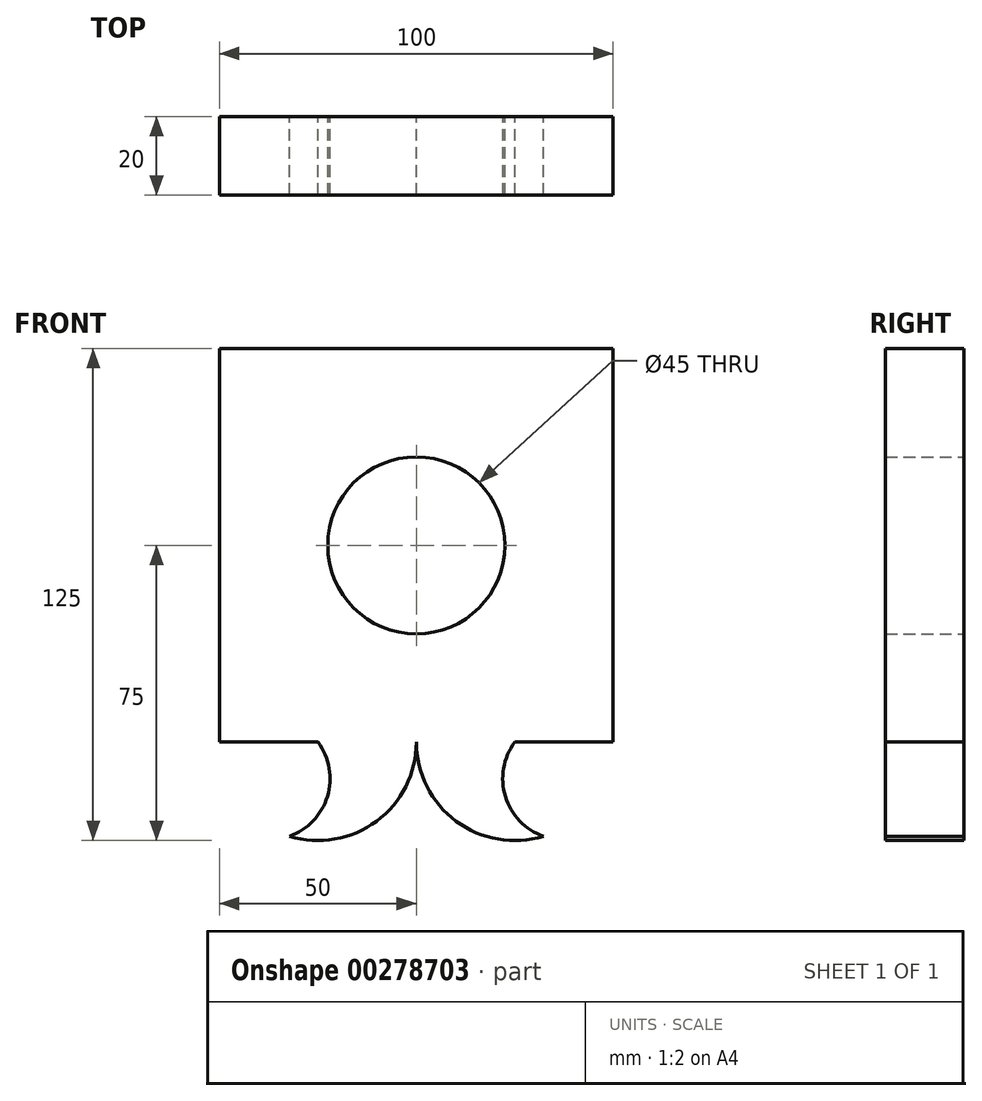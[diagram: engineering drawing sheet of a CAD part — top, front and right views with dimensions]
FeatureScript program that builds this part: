
annotation { "Feature Type Name" : "Feature", "Feature Type Description" : "" }
export const myFeature = defineFeature(function(context is Context, id is Id, definition is map)
    precondition{}
    {
        {
            var Q0;
            Q0=qCreatedBy(makeId("Front.planeOp"),FACE);
            var sketch = newSketch(context, id + "F0", { "sketchPlane" : qUnion([Q0])});
            skLineSegment(sketch, "E0.bottom", {"start": v(-40, 50) * mm, "end": v(40, 50) * mm});
            skLineSegment(sketch, "E0.top", {"start": v(-40, -50) * mm, "end": v(50, -50) * mm});
            skLineSegment(sketch, "E0.left", {"start": v(-50, 40) * mm, "end": v(-50, -40) * mm});
            skLineSegment(sketch, "E0.right", {"start": v(50, 40) * mm, "end": v(50, -40) * mm});
            skPoint(sketch, "E1.visualSharp", {"position": v(-50, 50) * mm});
            skPoint(sketch, "E2.visualSharp", {"position": v(50, 50) * mm});
            skPoint(sketch, "E3.visualSharp", {"position": v(50, -50) * mm});
            skPoint(sketch, "E4.visualSharp", {"position": v(-50, -50) * mm});
            skCircle(sketch, "E5", {"center": v(0, 0) * mm, "radius": 22.5 * mm});
            skLineSegment(sketch, "E6", {"start": v(50, 40) * mm, "end": v(50, 50) * mm});
            skLineSegment(sketch, "E7", {"start": v(37.5, 50) * mm, "end": v(50, 50) * mm});
            skLineSegment(sketch, "E8", {"start": v(-40, 50) * mm, "end": v(-50, 50) * mm});
            skLineSegment(sketch, "E9", {"start": v(-50, 40) * mm, "end": v(-50, 50) * mm});
            skLineSegment(sketch, "E10", {"start": v(-50, -41.98) * mm, "end": v(-50, -50) * mm});
            skLineSegment(sketch, "E11", {"start": v(-40, -50) * mm, "end": v(-50, -50) * mm});
            skLineSegment(sketch, "E12", {"start": v(-50, -41.98) * mm, "end": v(-50, -40) * mm});
            skLineSegment(sketch, "E13", {"start": v(50, -50) * mm, "end": v(50, -50) * mm});
            skLineSegment(sketch, "E14", {"start": v(50, -50) * mm, "end": v(50, -40) * mm});
            skLineSegment(sketch, "E15.MirrorCS", {"start": v(50, -41.98) * mm, "end": v(50, -50) * mm});
            skArc(sketch, "E16.MirrorCS", {"start": v(50, -50) * mm, "mid": v(25, -75) * mm, "end": v(0, -50) * mm});
            skLineSegment(sketch, "E17.MirrorCS", {"start": v(40, -50) * mm, "end": v(50, -50) * mm});
            skLineSegment(sketch, "E18.MirrorCS", {"start": v(40, -50) * mm, "end": v(-50, -50) * mm});
            skArc(sketch, "E19", {"start": v(-50, -50) * mm, "mid": v(-25, -75) * mm, "end": v(0, -50) * mm});
            skArc(sketch, "E20", {"start": v(-50, -50) * mm, "mid": v(-37.5, -74.82) * mm, "end": v(-25, -50) * mm});
            skArc(sketch, "E21", {"start": v(25, -50) * mm, "mid": v(37.5, -74.8) * mm, "end": v(50, -50) * mm});
            skSolve(sketch);
        }
        {
            var Q0;
            {var subQ0=sQuery(id+"F0.wireOp",EDGE,"E18.MirrorCS");var subQ5=sQuery(id+"F0.wireOp",EDGE,"f36f585f-f47f-4796-8ffd-381910e5da09");var subQ6=makeQuery(id+"F0.imprint","INTERSECT",VERTEX,{"disambiguationData":[OD(1.0)],"derivedFrom":[subQ0,subQ5]});Q0=makeQuery(id+"F0.imprint","IMPRINT",FACE,{"disambiguationData":[TD([[makeQuery(id+"F0.imprint","IMPRINT",EDGE,{"disambiguationData":[TD([[subQ6,-1.0]])],"derivedFrom":subQ5}),-1.0]])]});}
            var Q1;
            {var subQ6=sQuery(id+"F0.wireOp",EDGE,"E0.bottom");Q1=makeQuery(id+"F0.imprint","IMPRINT",FACE,{"disambiguationData":[TD([[makeQuery(id+"F0.imprint","IMPRINT",EDGE,{"derivedFrom":subQ6}),-1.0]])]});}
            var Q2;
            {var subQ1=sQuery(id+"F0.wireOp",EDGE,"E18.MirrorCS");var subQ3=sQuery(id+"F0.wireOp",EDGE,"E20");var subQ4=makeQuery(id+"F0.imprint","INTERSECT",VERTEX,{"derivedFrom":[subQ1,subQ3]});Q2=makeQuery(id+"F0.imprint","IMPRINT",FACE,{"disambiguationData":[TD([[makeQuery(id+"F0.imprint","IMPRINT",EDGE,{"disambiguationData":[TD([[subQ4,1.0]])],"derivedFrom":subQ3}),-1.0]])]});}
            var Q3;
            {var subQ0=sQuery(id+"F0.wireOp",EDGE,"E18.MirrorCS");var subQ3=sQuery(id+"F0.wireOp",EDGE,"E21");var subQ5=makeQuery(id+"F0.imprint","INTERSECT",VERTEX,{"derivedFrom":[subQ0,subQ3]});Q3=makeQuery(id+"F0.imprint","IMPRINT",FACE,{"disambiguationData":[TD([[makeQuery(id+"F0.imprint","IMPRINT",EDGE,{"disambiguationData":[TD([[subQ5,-1.0]])],"derivedFrom":subQ3}),-1.0]])]});}
            extrude(context, id + "F1", {"entities" : qUnion([Q0, Q1, Q2, Q3]), "depth" : 20 * mm});
        }
    });
